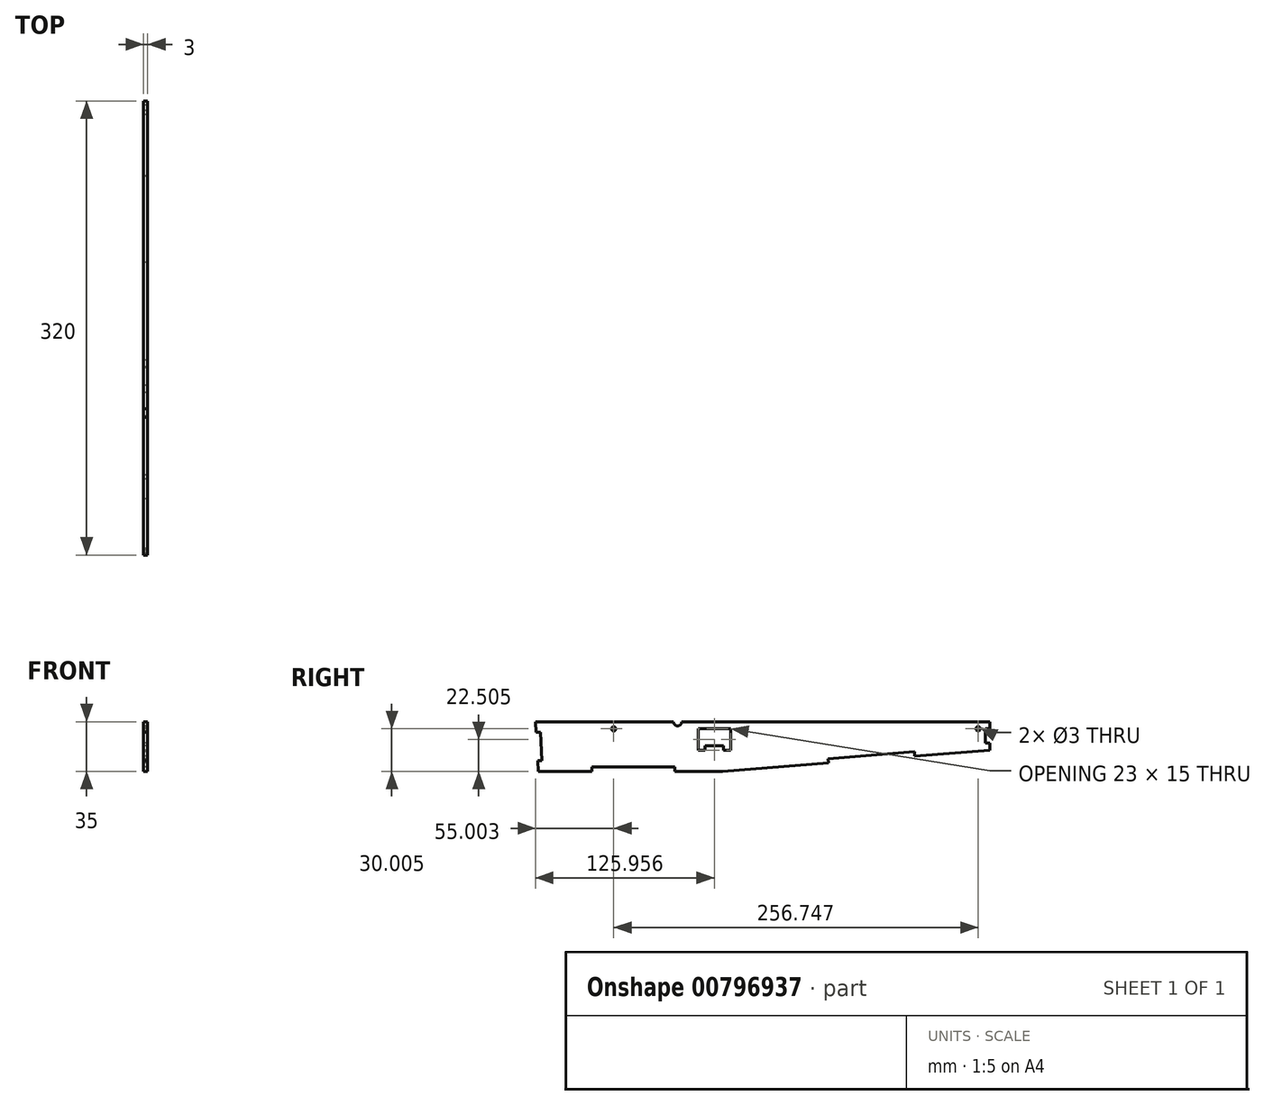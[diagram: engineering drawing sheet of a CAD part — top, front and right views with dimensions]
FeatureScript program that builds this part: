
annotation { "Feature Type Name" : "Feature", "Feature Type Description" : "" }
export const myFeature = defineFeature(function(context is Context, id is Id, definition is map)
    precondition{}
    {
        {
            var Q0;
            Q0=qCreatedBy(makeId("Right.planeOp"),FACE);
            var sketch = newSketch(context, id + "F0", { "sketchPlane" : qUnion([Q0])});
            skLineSegment(sketch, "E0", {"start": v(-143.84, -0.53) * mm, "end": v(-106.13, -0.53) * mm});
            skLineSegment(sketch, "E1", {"start": v(-145.68, 34.47) * mm, "end": v(-145.29, 26.99) * mm});
            skLineSegment(sketch, "E2", {"start": v(-144.24, 7.01) * mm, "end": v(-143.84, -0.53) * mm});
            skLineSegment(sketch, "E3", {"start": v(-145.29, 26.99) * mm, "end": v(-142.19, 27.15) * mm});
            skLineSegment(sketch, "E4", {"start": v(-144.24, 7.01) * mm, "end": v(-141.14, 7.17) * mm});
            skLineSegment(sketch, "E5", {"start": v(-142.19, 27.15) * mm, "end": v(-141.14, 7.17) * mm});
            skLineSegment(sketch, "E6", {"start": v(-85.68, 34.47) * mm, "end": v(-145.68, 34.47) * mm});
            skLineSegment(sketch, "E7", {"start": v(-13.84, -0.53) * mm, "end": v(60.66, 5.41) * mm});
            skLineSegment(sketch, "E8", {"start": v(-47.58, -0.53) * mm, "end": v(-13.84, -0.53) * mm});
            skLineSegment(sketch, "E9", {"start": v(121.38, 10.25) * mm, "end": v(174.32, 14.47) * mm});
            skLineSegment(sketch, "E10", {"start": v(-106.13, 2.57) * mm, "end": v(-47.58, 2.57) * mm});
            skLineSegment(sketch, "E11", {"start": v(-47.58, 2.57) * mm, "end": v(-47.58, -0.53) * mm});
            skLineSegment(sketch, "E12", {"start": v(60.66, 5.41) * mm, "end": v(60.42, 8.4) * mm});
            skLineSegment(sketch, "E13", {"start": v(121.14, 13.26) * mm, "end": v(121.38, 10.25) * mm});
            skLineSegment(sketch, "E14", {"start": v(60.42, 8.4) * mm, "end": v(121.14, 13.26) * mm});
            skLineSegment(sketch, "E15", {"start": v(-106.13, 2.57) * mm, "end": v(-106.13, -0.53) * mm});
            skLineSegment(sketch, "E16", {"start": v(174.32, 34.47) * mm, "end": v(164.32, 34.47) * mm});
            skCircle(sketch, "E17", {"center": v(-90.68, 29.47) * mm, "radius": 1.5 * mm});
            skCircle(sketch, "E18", {"center": v(166.07, 29.47) * mm, "radius": 1.5 * mm});
            skLineSegment(sketch, "E19", {"start": v(-85.68, 34.47) * mm, "end": v(-48.59, 34.47) * mm});
            skLineSegment(sketch, "E20", {"start": v(-42.77, 34.47) * mm, "end": v(164.32, 34.47) * mm});
            skArc(sketch, "E21", {"start": v(-48.59, 34.47) * mm, "mid": v(-45.68, 31.56) * mm, "end": v(-42.77, 34.47) * mm});
            skLineSegment(sketch, "E22.bottom", {"start": v(-31.22, 29.47) * mm, "end": v(-8.22, 29.47) * mm});
            skLineSegment(sketch, "E22.left", {"start": v(-31.22, 29.47) * mm, "end": v(-31.22, 17.47) * mm});
            skLineSegment(sketch, "E22.right", {"start": v(-8.22, 29.47) * mm, "end": v(-8.22, 17.47) * mm});
            skLineSegment(sketch, "E23", {"start": v(-31.22, 17.47) * mm, "end": v(-31.22, 14.47) * mm});
            skLineSegment(sketch, "E24", {"start": v(-31.22, 14.47) * mm, "end": v(-26.22, 14.47) * mm});
            skLineSegment(sketch, "E25", {"start": v(-26.22, 14.47) * mm, "end": v(-26.22, 17.47) * mm});
            skLineSegment(sketch, "E26", {"start": v(-8.22, 17.47) * mm, "end": v(-8.22, 14.47) * mm});
            skLineSegment(sketch, "E27", {"start": v(-8.22, 14.47) * mm, "end": v(-13.22, 14.47) * mm});
            skLineSegment(sketch, "E28", {"start": v(-13.22, 14.47) * mm, "end": v(-13.22, 17.47) * mm});
            skLineSegment(sketch, "E29", {"start": v(-26.22, 17.47) * mm, "end": v(-13.22, 17.47) * mm});
            skLineSegment(sketch, "E30", {"start": v(174.32, 34.47) * mm, "end": v(174.32, 29.47) * mm});
            skLineSegment(sketch, "E31", {"start": v(174.32, 29.47) * mm, "end": v(171.22, 29.47) * mm});
            skLineSegment(sketch, "E32", {"start": v(171.22, 29.47) * mm, "end": v(171.22, 19.47) * mm});
            skLineSegment(sketch, "E33", {"start": v(171.22, 19.47) * mm, "end": v(174.32, 19.47) * mm});
            skLineSegment(sketch, "E34", {"start": v(174.32, 19.47) * mm, "end": v(174.32, 14.47) * mm});
            skSolve(sketch);
        }
        {
            var Q0;
            Q0 = qSketchRegion(id + "F0", true);
            extrude(context, id + "F1", {"entities" : qUnion([Q0]), "depth" : 3 * mm, "offsetDistance" : 25 * mm});
        }
    });
